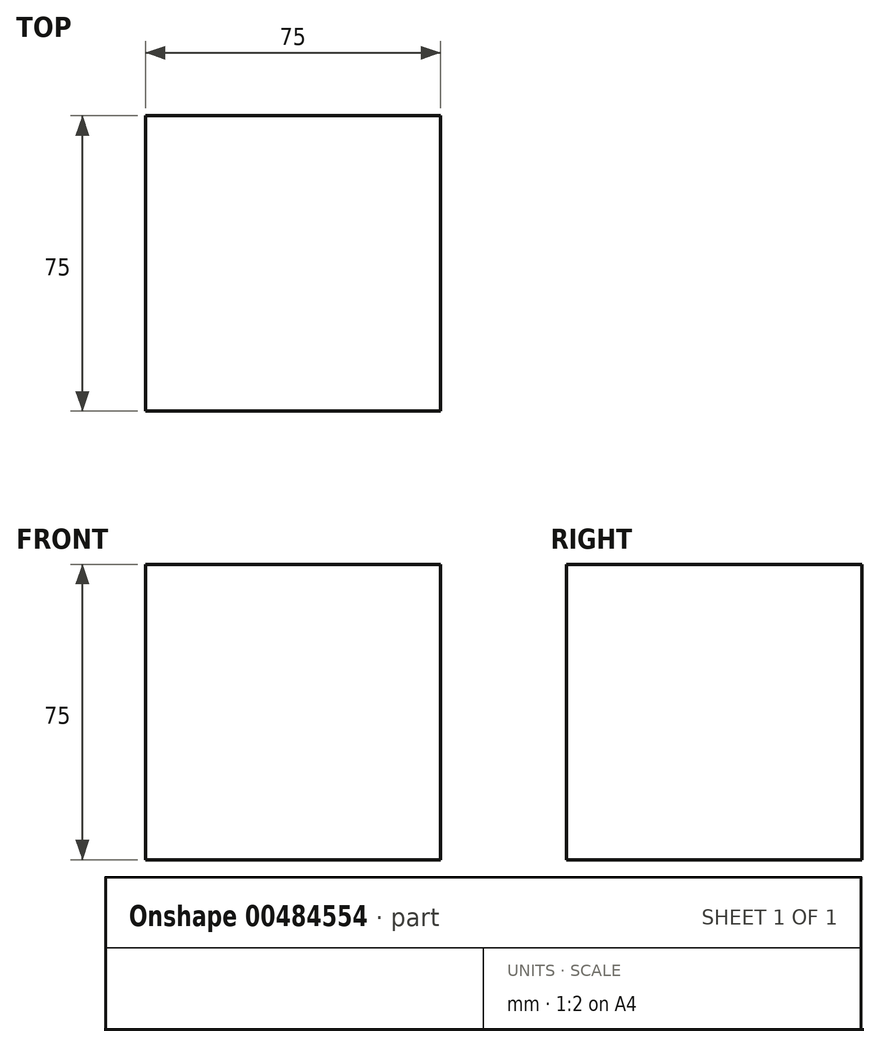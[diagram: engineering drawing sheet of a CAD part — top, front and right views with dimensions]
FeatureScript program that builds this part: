
annotation { "Feature Type Name" : "Feature", "Feature Type Description" : "" }
export const myFeature = defineFeature(function(context is Context, id is Id, definition is map)
    precondition{}
    {
        {
            var Q0;
            Q0=qCreatedBy(makeId("Top.planeOp"),FACE);
            var sketch = newSketch(context, id + "F0", { "sketchPlane" : qUnion([Q0])});
            skLineSegment(sketch, "E0.bottom", {"start": v(37.5, -37.5) * mm, "end": v(-37.5, -37.5) * mm});
            skLineSegment(sketch, "E0.top", {"start": v(37.5, 37.5) * mm, "end": v(-37.5, 37.5) * mm});
            skLineSegment(sketch, "E0.left", {"start": v(37.5, -37.5) * mm, "end": v(37.5, 37.5) * mm});
            skLineSegment(sketch, "E0.right", {"start": v(-37.5, -37.5) * mm, "end": v(-37.5, 37.5) * mm});
            skPoint(sketch, "E0.middle", {"position": v(0, 0) * mm});
            skSolve(sketch);
        }
        {
            var Q0;
            Q0=qSketchRegion(id+"F0",true);
            extrude(context, id + "F1", {"entities" : qUnion([Q0]), "depth" : 75 * mm});
        }
    });
